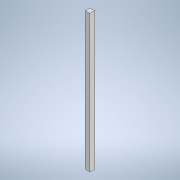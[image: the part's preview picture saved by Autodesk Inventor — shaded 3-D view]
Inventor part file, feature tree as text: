
AUTODESK INVENTOR PART (.ipt)
format: ipt  version: 2021 (Build 250183000, 183)  size: 94,208 bytes
history: native  units: mm
features: extrude x1, sketch x1
ambient origin geometry x8: Origin, YZ Plane, XZ Plane, XY Plane, X Axis, Y Axis, Z Axis, Center Point
bodies: Solid1 (feature_tree)
feature tree (2):
  extrude  "Extrusion1"  Depth=13.0mm
  sketch  "Sketch1"  dims[d0=13.0mm d1=13.0mm d2=379.0mm d3=0.0mm d4=0.5mm d5=0.872665mm d6=0.5mm d7=0.872665mm]
